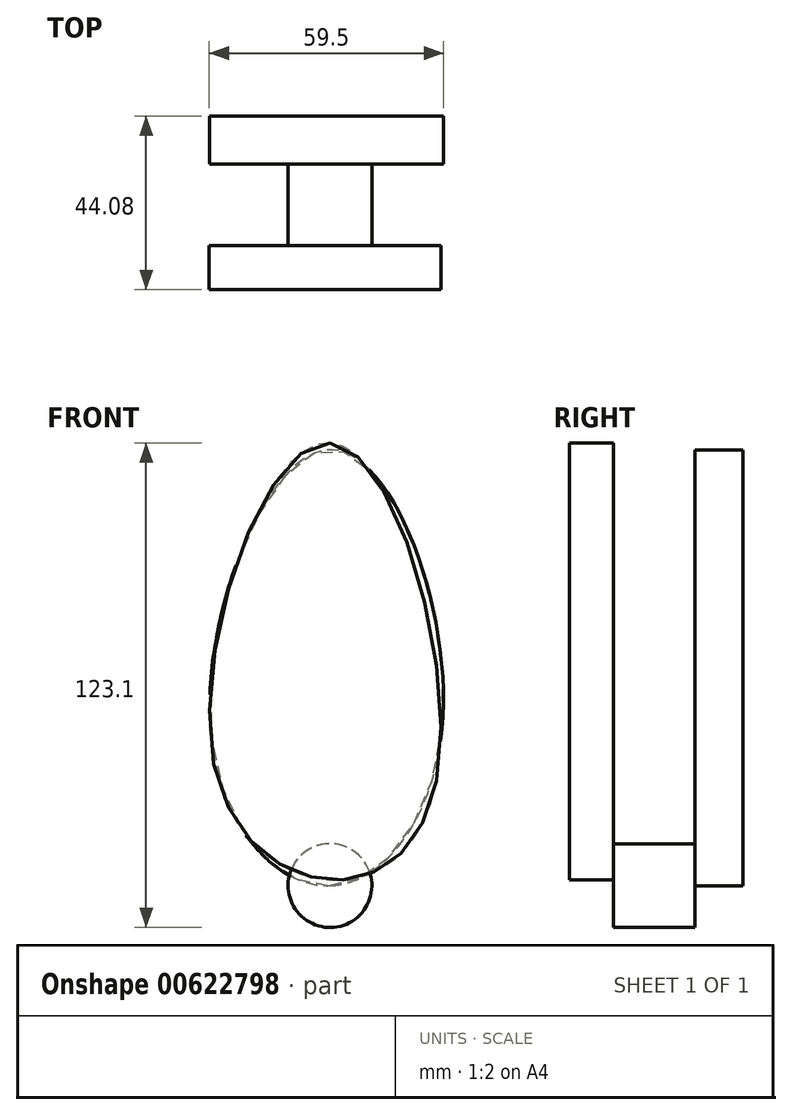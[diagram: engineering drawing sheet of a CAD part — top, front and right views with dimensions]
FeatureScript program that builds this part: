
annotation { "Feature Type Name" : "Feature", "Feature Type Description" : "" }
export const myFeature = defineFeature(function(context is Context, id is Id, definition is map)
    precondition{}
    {
        {
            var Q0;
            Q0=qCreatedBy(makeId("Front.planeOp"),FACE);
            var sketch = newSketch(context, id + "F0", { "sketchPlane" : qUnion([Q0])});
            skFitSpline(sketch, "E0", {"points": [v(0, 60.65) * mm, v(-30.2, -16.6) * mm, v(0, -50.32) * mm, v(27.28, -23.94) * mm, v(0, 60.65) * mm]});
            skSolve(sketch);
        }
        {
            var Q0;
            Q0=makeQuery(id+"F0.imprint","IMPRINT",FACE,{"disambiguationData":[TD([[makeQuery(id+"F0.imprint","IMPRINT",EDGE,{"derivedFrom":sQuery(id+"F0.wireOp",EDGE,"E0")}),1.0]])]});
            extrude(context, id + "F1", {"entities" : qUnion([Q0]), "depth" : 11.13 * mm, "offsetDistance" : 25.4 * mm});
        }
        {
            var Q0;
            Q0=makeQuery(id+"F1.opExtrude","CAP_FACE",FACE,{"disambiguationData":[OSD([sQuery(id+"F0.wireOp",EDGE,"E0")])],"isStart":true});
            var sketch = newSketch(context, id + "F2", { "sketchPlane" : qUnion([Q0])});
            skCircle(sketch, "E1", {"center": v(0, 41.87) * mm, "radius": 4.86 * mm});
            skSolve(sketch);
        }
        {
            var Q0;
            Q0=sQuery(id+"F2.wireOp",EDGE,"E1");
            extrude(context, id + "F3", {"bodyType" : ToolBodyType.SURFACE, "surfaceEntities" : qUnion([Q0]), "depth" : 12.24 * mm, "offsetDistance" : 25.4 * mm});
        }
        {
            var Q0;
            Q0=qCreatedBy(makeId("Front.planeOp"),FACE);
            var sketch = newSketch(context, id + "F4", { "sketchPlane" : qUnion([Q0])});
            skFitSpline(sketch, "E2", {"points": [v(0, 58.28) * mm, v(28.46, -10.65) * mm, v(0, -50.33) * mm, v(-29.9, -14.57) * mm, v(0, 58.28) * mm]});
            skSolve(sketch);
        }
        {
            var Q0;
            Q0=makeQuery(id+"F4.imprint","IMPRINT",FACE,{"disambiguationData":[TD([[makeQuery(id+"F4.imprint","IMPRINT",EDGE,{"derivedFrom":sQuery(id+"F4.wireOp",EDGE,"E2")}),-1.0]])]});
            var sketch = newSketch(context, id + "F5", { "sketchPlane" : qUnion([Q0])});
            skCircle(sketch, "E3", {"center": v(0, -51.79) * mm, "radius": 10.64 * mm});
            skSolve(sketch);
        }
        {
            var Q0;
            {var subQ0=sQuery(id+"F5.wireOp",EDGE,"E3");var subQ1=makeQuery(id+"F4.imprint","IMPRINT",EDGE,{"derivedFrom":sQuery(id+"F4.wireOp",EDGE,"E2")});var subQ2=makeQuery(id+"F5.imprint","INTERSECT",VERTEX,{"disambiguationData":[OD(0.0)],"derivedFrom":[subQ1,subQ0]});Q0=makeQuery(id+"F5.imprint","IMPRINT",FACE,{"disambiguationData":[TD([[makeQuery(id+"F5.imprint","IMPRINT",EDGE,{"disambiguationData":[TD([[subQ2,-1.0]])],"derivedFrom":subQ0}),1.0]])]});}
            var Q1;
            {var subQ0=sQuery(id+"F5.wireOp",EDGE,"E3");var subQ1=makeQuery(id+"F4.imprint","IMPRINT",EDGE,{"derivedFrom":sQuery(id+"F4.wireOp",EDGE,"E2")});var subQ2=makeQuery(id+"F5.imprint","INTERSECT",VERTEX,{"disambiguationData":[OD(0.0)],"derivedFrom":[subQ1,subQ0]});Q1=makeQuery(id+"F5.imprint","IMPRINT",FACE,{"disambiguationData":[TD([[makeQuery(id+"F5.imprint","IMPRINT",EDGE,{"disambiguationData":[TD([[subQ2,1.0]])],"derivedFrom":subQ0}),1.0]])]});}
            extrude(context, id + "F6", {"entities" : qUnion([Q0, Q1]), "operationType" : NewBodyOperationType.ADD, "oppositeDirection" : true, "depth" : 20.8 * mm, "offsetDistance" : 25.4 * mm});
        }
        {
            var Q0;
            Q0=makeQuery(id+"F6.opExtrude","CAP_FACE",FACE,{"disambiguationData":[OSD([sQuery(id+"F5.wireOp",EDGE,"E3")])],"isStart":false});
            var sketch = newSketch(context, id + "F7", { "sketchPlane" : qUnion([Q0])});
            skFitSpline(sketch, "E4", {"points": [v(0, -51.79) * mm, v(-28.66, -9.96) * mm, v(0, 58.95) * mm, v(30.3, -12.9) * mm, v(0, -51.79) * mm]});
            skSolve(sketch);
        }
        {
            var Q0;
            {var subQ0=sQuery(id+"F7.wireOp",EDGE,"E4");var subQ1=makeQuery(id+"F6.opExtrude","CAP_EDGE",EDGE,{"disambiguationData":[OSD([sQuery(id+"F5.wireOp",EDGE,"E3")])],"isStart":false});var subQ2=makeQuery(id+"F7.imprint","INTERSECT",VERTEX,{"disambiguationData":[OD(0.0)],"derivedFrom":[subQ1,subQ0]});Q0=makeQuery(id+"F7.imprint","IMPRINT",FACE,{"disambiguationData":[TD([[makeQuery(id+"F7.imprint","IMPRINT",EDGE,{"disambiguationData":[TD([[subQ2,1.0]])],"derivedFrom":subQ0}),-1.0]])]});}
            var Q1;
            Q1 = qSketchRegion(id + "F7", true);
            var Q2;
            {var subQ0=sQuery(id+"F7.wireOp",EDGE,"E4");var subQ1=makeQuery(id+"F6.opExtrude","CAP_EDGE",EDGE,{"disambiguationData":[OSD([sQuery(id+"F5.wireOp",EDGE,"E3")])],"isStart":false});var subQ2=makeQuery(id+"F7.imprint","INTERSECT",VERTEX,{"disambiguationData":[OD(0.0)],"derivedFrom":[subQ1,subQ0]});Q2=makeQuery(id+"F7.imprint","IMPRINT",FACE,{"disambiguationData":[TD([[makeQuery(id+"F7.imprint","IMPRINT",EDGE,{"disambiguationData":[TD([[subQ2,-1.0]])],"derivedFrom":subQ0}),-1.0]])]});}
            extrude(context, id + "F8", {"entities" : qUnion([Q0, Q1, Q2]), "operationType" : NewBodyOperationType.ADD, "depth" : 12.16 * mm, "offsetDistance" : 25.4 * mm});
        }
        {
            var Q0;
            Q0=qCreatedBy(makeId("Top.planeOp"),FACE);
            var sketch = newSketch(context, id + "F9", { "sketchPlane" : qUnion([Q0])});
            skCircle(sketch, "E5", {"center": v(0, 13.64) * mm, "radius": 3.72 * mm});
            skSolve(sketch);
        }
        {
            var Q0;
            Q0=sQuery(id+"F9.wireOp",EDGE,"E5");
            extrude(context, id + "F10", {"bodyType" : ToolBodyType.SURFACE, "surfaceEntities" : qUnion([Q0]), "oppositeDirection" : true, "depth" : 153.87 * mm, "offsetDistance" : 25.4 * mm});
        }
    });
